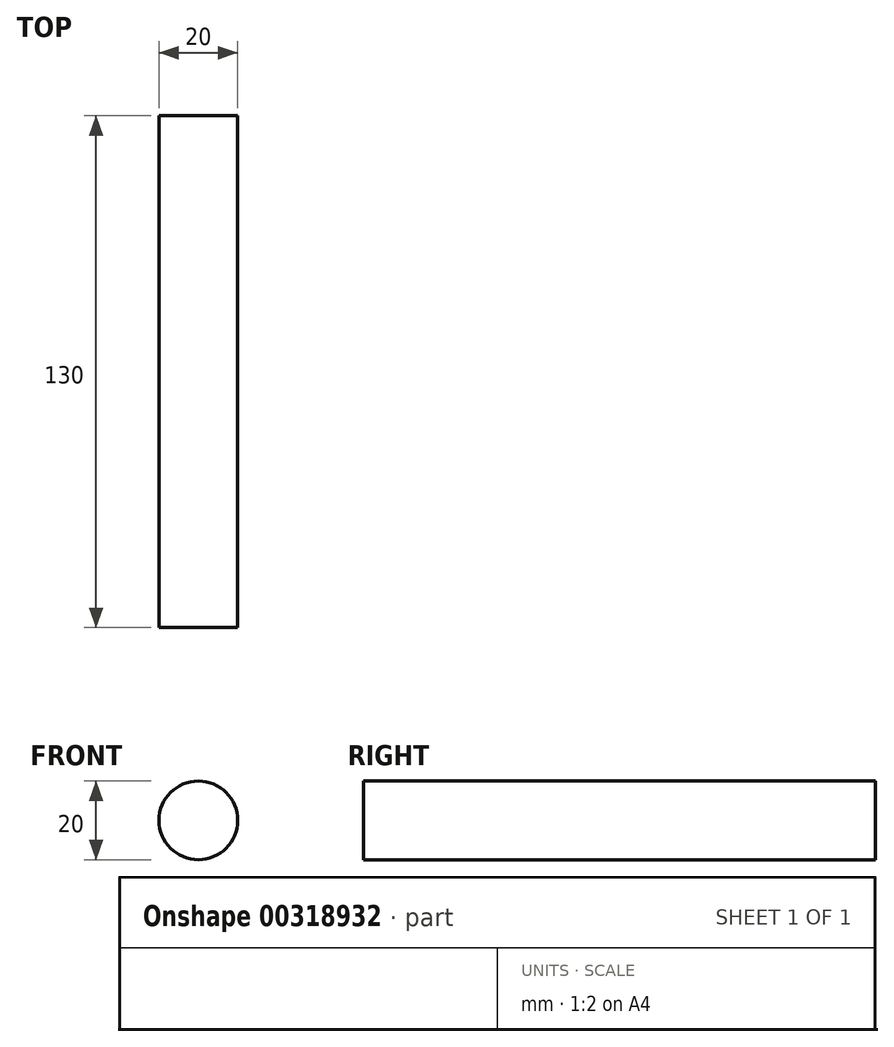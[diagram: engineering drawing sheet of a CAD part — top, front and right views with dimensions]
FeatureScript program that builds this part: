
annotation { "Feature Type Name" : "Feature", "Feature Type Description" : "" }
export const myFeature = defineFeature(function(context is Context, id is Id, definition is map)
    precondition{}
    {
        {
            var Q0;
            Q0=qCreatedBy(makeId("Front.planeOp"),FACE);
            var sketch = newSketch(context, id + "F0", { "sketchPlane" : qUnion([Q0])});
            skCircle(sketch, "E0", {"center": v(0, 0) * mm, "radius": 10 * mm});
            skSolve(sketch);
        }
        {
            var Q0;
            Q0 = qSketchRegion(id + "F0", true);
            extrude(context, id + "F1", {"entities" : qUnion([Q0]), "depth" : 130 * mm, "offsetDistance" : 25 * mm});
        }
    });
